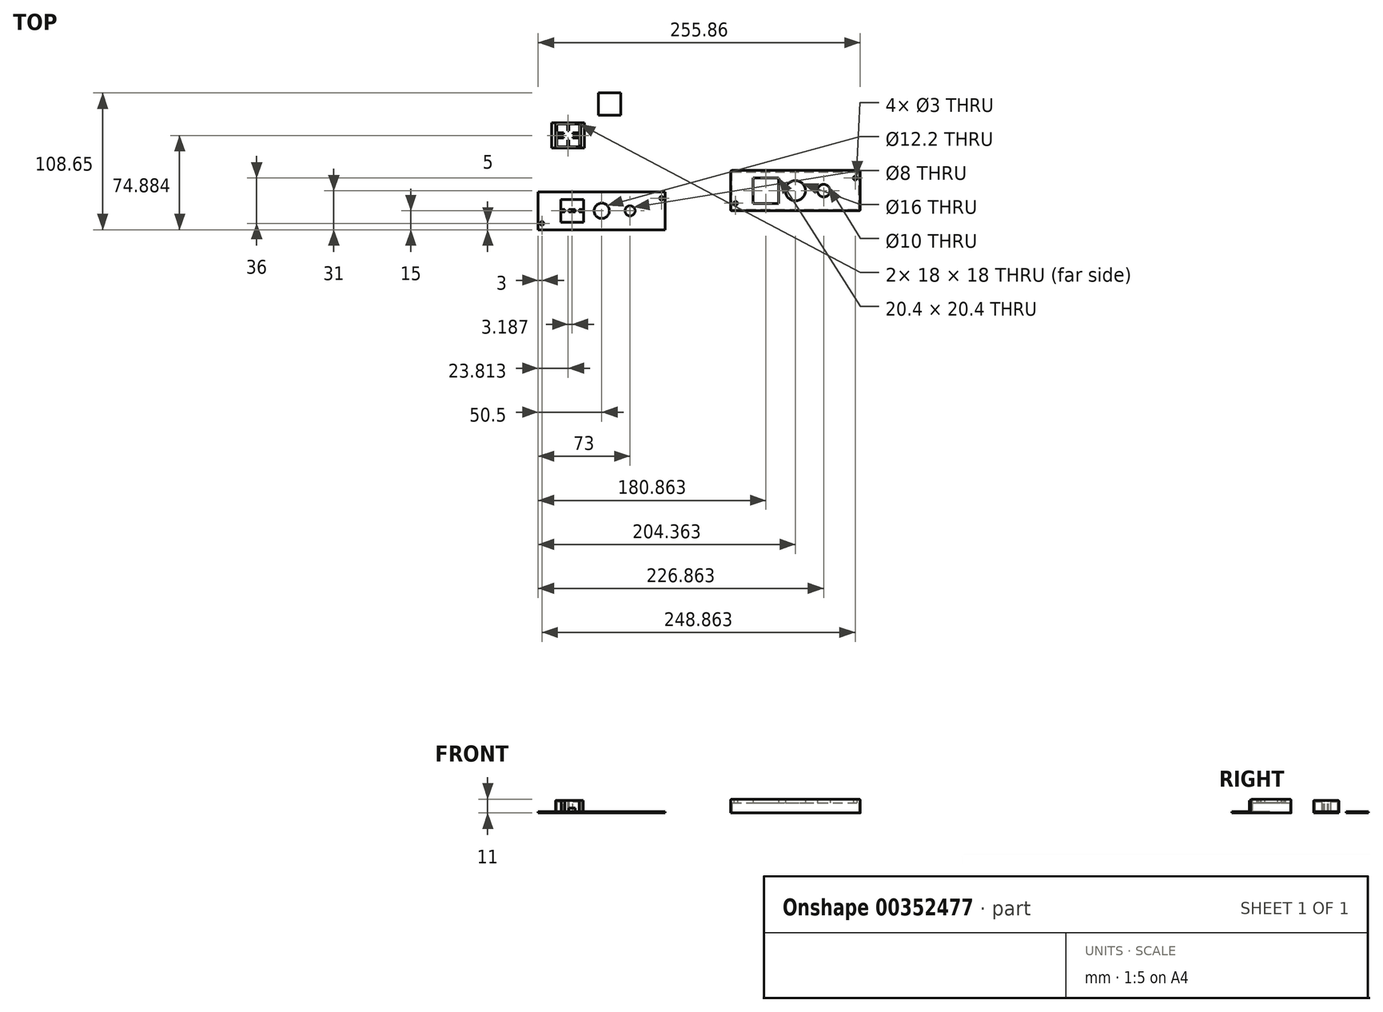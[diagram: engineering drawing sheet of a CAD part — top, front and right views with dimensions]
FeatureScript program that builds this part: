
annotation { "Feature Type Name" : "Feature", "Feature Type Description" : "" }
export const myFeature = defineFeature(function(context is Context, id is Id, definition is map)
    precondition{}
    {
        {
            var Q0;
            Q0=qCreatedBy(makeId("Top.planeOp"),FACE);
            var sketch = newSketch(context, id + "F0", { "sketchPlane" : qUnion([Q0])});
            skLineSegment(sketch, "E0.bottom", {"start": v(42.5, -14) * mm, "end": v(-42.5, -14) * mm, "construction": true});
            skLineSegment(sketch, "E0.top", {"start": v(42.5, 14) * mm, "end": v(-42.5, 14) * mm, "construction": true});
            skLineSegment(sketch, "E0.left", {"start": v(42.5, -14) * mm, "end": v(42.5, 14) * mm, "construction": true});
            skLineSegment(sketch, "E0.right", {"start": v(-42.5, -14) * mm, "end": v(-42.5, 14) * mm, "construction": true});
            skPoint(sketch, "E0.middle", {"position": v(0, 0) * mm});
            skCircle(sketch, "E1", {"center": v(-47.5, -10) * mm, "radius": 1.5 * mm});
            skCircle(sketch, "E2", {"center": v(47.5, 10) * mm, "radius": 1.5 * mm});
            skLineSegment(sketch, "E3.bottom", {"start": v(-50.5, 15) * mm, "end": v(50.5, 15) * mm});
            skLineSegment(sketch, "E3.top", {"start": v(-50.5, -15) * mm, "end": v(50.5, -15) * mm});
            skLineSegment(sketch, "E3.left", {"start": v(-50.5, 15) * mm, "end": v(-50.5, -15) * mm});
            skLineSegment(sketch, "E3.right", {"start": v(50.5, 15) * mm, "end": v(50.5, -15) * mm});
            skLineSegment(sketch, "E4.bottom", {"start": v(-32.5, 9) * mm, "end": v(-14.5, 9) * mm});
            skLineSegment(sketch, "E4.top", {"start": v(-32.5, -9) * mm, "end": v(-14.5, -9) * mm});
            skLineSegment(sketch, "E4.left", {"start": v(-32.5, 9) * mm, "end": v(-32.5, 1) * mm});
            skLineSegment(sketch, "E4.right", {"start": v(-14.5, 9) * mm, "end": v(-14.5, -9) * mm});
            skLineSegment(sketch, "E5.bottom", {"start": v(-29.25, 9) * mm, "end": v(-27.25, 9) * mm});
            skLineSegment(sketch, "E5.top", {"start": v(-29.25, -9) * mm, "end": v(-27.25, -9) * mm});
            skLineSegment(sketch, "E5.left", {"start": v(-29.25, 9) * mm, "end": v(-29.25, 1) * mm});
            skLineSegment(sketch, "E5.right", {"start": v(-27.25, 9) * mm, "end": v(-27.25, 1) * mm});
            skLineSegment(sketch, "E6.bottom", {"start": v(-19.75, 9) * mm, "end": v(-17.75, 9) * mm});
            skLineSegment(sketch, "E6.top", {"start": v(-19.75, -9) * mm, "end": v(-17.75, -9) * mm});
            skLineSegment(sketch, "E6.left", {"start": v(-19.75, 9) * mm, "end": v(-19.75, 1) * mm});
            skLineSegment(sketch, "E6.right", {"start": v(-17.75, 9) * mm, "end": v(-17.75, 1) * mm});
            skLineSegment(sketch, "E7.bottom", {"start": v(-32.5, 1) * mm, "end": v(-29.25, 1) * mm});
            skLineSegment(sketch, "E7.top", {"start": v(-32.5, -1) * mm, "end": v(-29.25, -1) * mm});
            skLineSegment(sketch, "E7.left", {"start": v(-32.5, 1) * mm, "end": v(-32.5, -1) * mm});
            skLineSegment(sketch, "E8.trimOffspring", {"start": v(-29.25, -1) * mm, "end": v(-29.25, -9) * mm});
            skLineSegment(sketch, "E9.trimOffspring", {"start": v(-27.25, 1) * mm, "end": v(-19.75, 1) * mm});
            skLineSegment(sketch, "E10.trimOffspring", {"start": v(-27.25, -1) * mm, "end": v(-27.25, -9) * mm});
            skLineSegment(sketch, "E11.trimOffspring", {"start": v(-27.25, -1) * mm, "end": v(-19.75, -1) * mm});
            skLineSegment(sketch, "E12.trimOffspring", {"start": v(-17.75, 1) * mm, "end": v(-14.5, 1) * mm});
            skLineSegment(sketch, "E13.trimOffspring", {"start": v(-17.75, -1) * mm, "end": v(-14.5, -1) * mm});
            skLineSegment(sketch, "E14.trimOffspring", {"start": v(-19.75, -1) * mm, "end": v(-19.75, -9) * mm});
            skLineSegment(sketch, "E15.trimOffspring", {"start": v(-17.75, -1) * mm, "end": v(-17.75, -9) * mm});
            skLineSegment(sketch, "E16.trimOffspring", {"start": v(-32.5, -1) * mm, "end": v(-32.5, -9) * mm});
            skCircle(sketch, "E17", {"center": v(0, 0) * mm, "radius": 6.1 * mm});
            skCircle(sketch, "E18", {"center": v(22.5, 0) * mm, "radius": 4 * mm});
            skSolve(sketch);
        }
        {
            var Q0;
            Q0=makeQuery(id+"F0.imprint","IMPRINT",FACE,{"disambiguationData":[TD([[makeQuery(id+"F0.imprint","IMPRINT",EDGE,{"derivedFrom":sQuery(id+"F0.wireOp",EDGE,"E1")}),-1.0]])]});
            var Q1;
            Q1=makeQuery(id+"F0.imprint","IMPRINT",FACE,{"disambiguationData":[TD([[makeQuery(id+"F0.imprint","IMPRINT",EDGE,{"derivedFrom":sQuery(id+"F0.wireOp",EDGE,"E5.bottom")}),-1.0]])]});
            extrude(context, id + "F1", {"entities" : qUnion([Q0, Q1]), "depth" : 1 * mm});
        }
        {
            var Q0;
            Q0=makeQuery(id+"F1.opExtrude","CAP_FACE",FACE,{"disambiguationData":[OSD([sQuery(id+"F0.wireOp",EDGE,"E1"),sQuery(id+"F0.wireOp",EDGE,"E2"),sQuery(id+"F0.wireOp",EDGE,"E3.bottom"),sQuery(id+"F0.wireOp",EDGE,"E3.top"),sQuery(id+"F0.wireOp",EDGE,"E3.left"),sQuery(id+"F0.wireOp",EDGE,"E3.right"),sQuery(id+"F0.wireOp",EDGE,"424KGZRB-5utR-a6Sk-f07y-1cyDiIB8TaRe"),sQuery(id+"F0.wireOp",EDGE,"xPdJMKwa-e6o6-zGCf-eMrl-vuys1Or93pA9"),sQuery(id+"F0.wireOp",EDGE,"E4.bottom"),sQuery(id+"F0.wireOp",EDGE,"E4.top"),sQuery(id+"F0.wireOp",EDGE,"E4.left"),sQuery(id+"F0.wireOp",EDGE,"E4.right"),sQuery(id+"F0.wireOp",EDGE,"E5.left"),sQuery(id+"F0.wireOp",EDGE,"E5.right"),sQuery(id+"F0.wireOp",EDGE,"E6.left"),sQuery(id+"F0.wireOp",EDGE,"E6.right"),sQuery(id+"F0.wireOp",EDGE,"E7.bottom"),sQuery(id+"F0.wireOp",EDGE,"E7.top"),sQuery(id+"F0.wireOp",EDGE,"E8.trimOffspring"),sQuery(id+"F0.wireOp",EDGE,"E9.trimOffspring"),sQuery(id+"F0.wireOp",EDGE,"E10.trimOffspring"),sQuery(id+"F0.wireOp",EDGE,"E11.trimOffspring"),sQuery(id+"F0.wireOp",EDGE,"E12.trimOffspring"),sQuery(id+"F0.wireOp",EDGE,"E13.trimOffspring"),sQuery(id+"F0.wireOp",EDGE,"E14.trimOffspring"),sQuery(id+"F0.wireOp",EDGE,"E15.trimOffspring"),sQuery(id+"F0.wireOp",EDGE,"E16.trimOffspring")])],"isStart":false});
            var sketch = newSketch(context, id + "F2", { "sketchPlane" : qUnion([Q0])});
            skLineSegment(sketch, "E19.bottom", {"start": v(-29.25, 1) * mm, "end": v(-32.25, 1) * mm});
            skLineSegment(sketch, "E19.top", {"start": v(-29.25, -1) * mm, "end": v(-32.25, -1) * mm});
            skLineSegment(sketch, "E19.left", {"start": v(-29.25, 1) * mm, "end": v(-29.25, -1) * mm});
            skLineSegment(sketch, "E19.right", {"start": v(-32.25, 1) * mm, "end": v(-32.25, -1) * mm});
            skLineSegment(sketch, "E20.bottom", {"start": v(-17.75, 1) * mm, "end": v(-14.75, 1) * mm});
            skLineSegment(sketch, "E20.top", {"start": v(-17.75, -1) * mm, "end": v(-14.75, -1) * mm});
            skLineSegment(sketch, "E20.left", {"start": v(-17.75, 1) * mm, "end": v(-17.75, -1) * mm});
            skLineSegment(sketch, "E20.right", {"start": v(-14.75, 1) * mm, "end": v(-14.75, -1) * mm});
            skSolve(sketch);
        }
        {
            var Q0;
            Q0 = qSketchRegion(id + "F2", true);
            extrude(context, id + "F3", {"entities" : qUnion([Q0]), "operationType" : NewBodyOperationType.ADD, "depth" : 9 * mm});
        }
        {
            var Q0;
            Q0=qCreatedBy(makeId("Top.planeOp"),FACE);
            var sketch = newSketch(context, id + "F4", { "sketchPlane" : qUnion([Q0])});
            skLineSegment(sketch, "E21.bottom", {"start": v(-36.69, 69.88) * mm, "end": v(-16.69, 69.88) * mm});
            skLineSegment(sketch, "E21.top", {"start": v(-36.69, 49.88) * mm, "end": v(-16.69, 49.88) * mm});
            skLineSegment(sketch, "E21.left", {"start": v(-36.69, 69.88) * mm, "end": v(-36.69, 49.88) * mm});
            skLineSegment(sketch, "E21.right", {"start": v(-16.69, 69.88) * mm, "end": v(-16.69, 49.88) * mm});
            skLineSegment(sketch, "E22.bottom", {"start": v(-2.69, 93.65) * mm, "end": v(15.11, 93.65) * mm});
            skLineSegment(sketch, "E22.top", {"start": v(-2.69, 75.85) * mm, "end": v(15.11, 75.85) * mm});
            skLineSegment(sketch, "E22.left", {"start": v(-2.69, 93.65) * mm, "end": v(-2.69, 75.85) * mm});
            skLineSegment(sketch, "E22.right", {"start": v(15.11, 93.65) * mm, "end": v(15.11, 75.85) * mm});
            skSolve(sketch);
        }
        {
            var Q0;
            Q0=makeQuery(id+"F4.imprint","IMPRINT",FACE,{"disambiguationData":[TD([[makeQuery(id+"F4.imprint","IMPRINT",EDGE,{"derivedFrom":sQuery(id+"F4.wireOp",EDGE,"E21.bottom")}),-1.0]])]});
            extrude(context, id + "F5", {"entities" : qUnion([Q0]), "depth" : 10 * mm});
        }
        {
            var Q0;
            Q0=makeQuery(id+"F5.opExtrude","CAP_FACE",FACE,{"disambiguationData":[OSD([sQuery(id+"F4.wireOp",EDGE,"E21.bottom"),sQuery(id+"F4.wireOp",EDGE,"E21.top"),sQuery(id+"F4.wireOp",EDGE,"E21.left"),sQuery(id+"F4.wireOp",EDGE,"E21.right")])],"isStart":true});
            shell(context, id + "F6", {"entities" : qUnion([Q0]), "thickness" : 1 * mm});
        }
        {
            var Q0;
            Q0=makeQuery(id+"F5.opExtrude","CAP_FACE",FACE,{"disambiguationData":[OSD([sQuery(id+"F4.wireOp",EDGE,"E21.bottom"),sQuery(id+"F4.wireOp",EDGE,"E21.top"),sQuery(id+"F4.wireOp",EDGE,"E21.left"),sQuery(id+"F4.wireOp",EDGE,"E21.right")])],"isStart":true});
            var sketch = newSketch(context, id + "F7", { "sketchPlane" : qUnion([Q0])});
            skLineSegment(sketch, "E23.bottom", {"start": v(-35.69, -57.88) * mm, "end": v(-27.19, -57.88) * mm});
            skLineSegment(sketch, "E23.top", {"start": v(-35.69, -58.58) * mm, "end": v(-27.19, -58.58) * mm});
            skLineSegment(sketch, "E23.left", {"start": v(-35.69, -57.88) * mm, "end": v(-35.69, -58.58) * mm});
            skLineSegment(sketch, "E23.right", {"start": v(-17.69, -57.88) * mm, "end": v(-17.69, -58.58) * mm});
            skLineSegment(sketch, "E24.bottom", {"start": v(-35.69, -61.18) * mm, "end": v(-27.19, -61.18) * mm});
            skLineSegment(sketch, "E24.top", {"start": v(-35.69, -61.88) * mm, "end": v(-27.19, -61.88) * mm});
            skLineSegment(sketch, "E24.left", {"start": v(-35.69, -61.18) * mm, "end": v(-35.69, -61.88) * mm});
            skLineSegment(sketch, "E24.right", {"start": v(-17.69, -61.18) * mm, "end": v(-17.69, -61.88) * mm});
            skLineSegment(sketch, "E25.bottom", {"start": v(-27.19, -50.88) * mm, "end": v(-26.19, -50.88) * mm});
            skLineSegment(sketch, "E25.top", {"start": v(-27.19, -68.88) * mm, "end": v(-26.19, -68.88) * mm});
            skLineSegment(sketch, "E25.left", {"start": v(-27.19, -50.88) * mm, "end": v(-27.19, -68.88) * mm});
            skLineSegment(sketch, "E25.right", {"start": v(-26.19, -50.88) * mm, "end": v(-26.19, -68.88) * mm});
            skLineSegment(sketch, "E26.trimOffspring", {"start": v(-26.19, -57.88) * mm, "end": v(-17.69, -57.88) * mm});
            skLineSegment(sketch, "E27.trimOffspring", {"start": v(-26.19, -58.58) * mm, "end": v(-17.69, -58.58) * mm});
            skLineSegment(sketch, "E28.trimOffspring", {"start": v(-26.19, -61.18) * mm, "end": v(-17.69, -61.18) * mm});
            skLineSegment(sketch, "E29.trimOffspring", {"start": v(-26.19, -61.88) * mm, "end": v(-17.69, -61.88) * mm});
            skSolve(sketch);
        }
        {
            var Q0;
            Q0 = qSketchRegion(id + "F7", true);
            extrude(context, id + "F8", {"entities" : qUnion([Q0]), "operationType" : NewBodyOperationType.ADD, "oppositeDirection" : true, "depth" : 9 * mm});
        }
        {
            var Q0;
            Q0=makeQuery(id+"F8.boolean.opBoolean","MERGE",FACE,{"derivedFrom":[makeQuery(id+"F5.opExtrude","CAP_FACE",FACE,{"disambiguationData":[OSD([sQuery(id+"F4.wireOp",EDGE,"E21.bottom"),sQuery(id+"F4.wireOp",EDGE,"E21.top"),sQuery(id+"F4.wireOp",EDGE,"E21.left"),sQuery(id+"F4.wireOp",EDGE,"E21.right")])],"isStart":true}),makeQuery(id+"F8.opExtrude","CAP_FACE",FACE,{"disambiguationData":[OSD([sQuery(id+"F7.wireOp",EDGE,"E23.bottom"),sQuery(id+"F7.wireOp",EDGE,"E23.top"),sQuery(id+"F7.wireOp",EDGE,"E23.left"),sQuery(id+"F7.wireOp",EDGE,"E23.right"),sQuery(id+"F7.wireOp",EDGE,"E24.bottom"),sQuery(id+"F7.wireOp",EDGE,"E24.top"),sQuery(id+"F7.wireOp",EDGE,"E24.left"),sQuery(id+"F7.wireOp",EDGE,"E24.right"),sQuery(id+"F7.wireOp",EDGE,"E25.bottom"),sQuery(id+"F7.wireOp",EDGE,"E25.top"),sQuery(id+"F7.wireOp",EDGE,"E25.left"),sQuery(id+"F7.wireOp",EDGE,"E25.right"),sQuery(id+"F7.wireOp",EDGE,"E26.trimOffspring"),sQuery(id+"F7.wireOp",EDGE,"E27.trimOffspring"),sQuery(id+"F7.wireOp",EDGE,"E28.trimOffspring"),sQuery(id+"F7.wireOp",EDGE,"E29.trimOffspring")])],"isStart":true})]});
            var sketch = newSketch(context, id + "F9", { "sketchPlane" : qUnion([Q0])});
            skLineSegment(sketch, "E30.bottom", {"start": v(-30.29, -56.28) * mm, "end": v(-23.09, -56.28) * mm});
            skLineSegment(sketch, "E30.top", {"start": v(-30.29, -63.48) * mm, "end": v(-23.09, -63.48) * mm});
            skLineSegment(sketch, "E30.left", {"start": v(-30.29, -56.28) * mm, "end": v(-30.29, -63.48) * mm});
            skLineSegment(sketch, "E30.right", {"start": v(-23.09, -56.28) * mm, "end": v(-23.09, -63.48) * mm});
            skSolve(sketch);
        }
        {
            var Q0;
            Q0 = qSketchRegion(id + "F9", true);
            extrude(context, id + "F10", {"entities" : qUnion([Q0]), "operationType" : NewBodyOperationType.REMOVE, "oppositeDirection" : true, "depth" : 9 * mm});
        }
        {
            var Q0;
            Q0=makeQuery(id+"F8.boolean.opBoolean","MERGE",FACE,{"derivedFrom":[makeQuery(id+"F5.opExtrude","CAP_FACE",FACE,{"disambiguationData":[OSD([sQuery(id+"F4.wireOp",EDGE,"E21.bottom"),sQuery(id+"F4.wireOp",EDGE,"E21.top"),sQuery(id+"F4.wireOp",EDGE,"E21.left"),sQuery(id+"F4.wireOp",EDGE,"E21.right")])],"isStart":true}),makeQuery(id+"F8.opExtrude","CAP_FACE",FACE,{"disambiguationData":[OSD([sQuery(id+"F7.wireOp",EDGE,"E23.bottom"),sQuery(id+"F7.wireOp",EDGE,"E23.top"),sQuery(id+"F7.wireOp",EDGE,"E23.left"),sQuery(id+"F7.wireOp",EDGE,"E23.right"),sQuery(id+"F7.wireOp",EDGE,"E24.bottom"),sQuery(id+"F7.wireOp",EDGE,"E24.top"),sQuery(id+"F7.wireOp",EDGE,"E24.left"),sQuery(id+"F7.wireOp",EDGE,"E24.right"),sQuery(id+"F7.wireOp",EDGE,"E25.bottom"),sQuery(id+"F7.wireOp",EDGE,"E25.top"),sQuery(id+"F7.wireOp",EDGE,"E25.left"),sQuery(id+"F7.wireOp",EDGE,"E25.right"),sQuery(id+"F7.wireOp",EDGE,"E26.trimOffspring"),sQuery(id+"F7.wireOp",EDGE,"E27.trimOffspring"),sQuery(id+"F7.wireOp",EDGE,"E28.trimOffspring"),sQuery(id+"F7.wireOp",EDGE,"E29.trimOffspring")])],"isStart":true})]});
            var sketch = newSketch(context, id + "F11", { "sketchPlane" : qUnion([Q0])});
            skLineSegment(sketch, "E31.bottom", {"start": v(-16.69, -69.88) * mm, "end": v(-13.69, -69.88) * mm});
            skLineSegment(sketch, "E31.top", {"start": v(-16.69, -49.88) * mm, "end": v(-13.69, -49.88) * mm});
            skLineSegment(sketch, "E31.left", {"start": v(-16.69, -69.88) * mm, "end": v(-16.69, -49.88) * mm});
            skLineSegment(sketch, "E31.right", {"start": v(-13.69, -69.88) * mm, "end": v(-13.69, -49.88) * mm});
            skLineSegment(sketch, "E32.bottom", {"start": v(-36.69, -69.88) * mm, "end": v(-39.69, -69.88) * mm});
            skLineSegment(sketch, "E32.top", {"start": v(-36.69, -49.88) * mm, "end": v(-39.69, -49.88) * mm});
            skLineSegment(sketch, "E32.left", {"start": v(-36.69, -69.88) * mm, "end": v(-36.69, -49.88) * mm});
            skLineSegment(sketch, "E32.right", {"start": v(-39.69, -69.88) * mm, "end": v(-39.69, -49.88) * mm});
            skSolve(sketch);
        }
        {
            var Q0;
            Q0=makeQuery(id+"F11.imprint","IMPRINT",FACE,{"disambiguationData":[TD([[makeQuery(id+"F11.imprint","IMPRINT",EDGE,{"derivedFrom":sQuery(id+"F11.wireOp",EDGE,"E32.bottom")}),-1.0]])]});
            var Q1;
            Q1=makeQuery(id+"F11.imprint","IMPRINT",FACE,{"disambiguationData":[TD([[makeQuery(id+"F11.imprint","IMPRINT",EDGE,{"derivedFrom":sQuery(id+"F11.wireOp",EDGE,"E31.bottom")}),1.0]])]});
            extrude(context, id + "F12", {"entities" : qUnion([Q0, Q1]), "operationType" : NewBodyOperationType.ADD, "oppositeDirection" : true, "depth" : 1 * mm});
        }
        {
            var Q0;
            Q0=makeQuery(id+"F5.opExtrude","CAP_FACE",FACE,{"disambiguationData":[OSD([sQuery(id+"F4.wireOp",EDGE,"E21.bottom"),sQuery(id+"F4.wireOp",EDGE,"E21.top"),sQuery(id+"F4.wireOp",EDGE,"E21.left"),sQuery(id+"F4.wireOp",EDGE,"E21.right")])],"isStart":false});
            var sketch = newSketch(context, id + "F13", { "sketchPlane" : qUnion([Q0])});
            skLineSegment(sketch, "E33.bottom", {"start": v(-35.69, 68.88) * mm, "end": v(-17.69, 68.88) * mm});
            skLineSegment(sketch, "E33.top", {"start": v(-35.69, 50.88) * mm, "end": v(-17.69, 50.88) * mm});
            skLineSegment(sketch, "E33.left", {"start": v(-35.69, 68.88) * mm, "end": v(-35.69, 50.88) * mm});
            skLineSegment(sketch, "E33.right", {"start": v(-17.69, 68.88) * mm, "end": v(-17.69, 50.88) * mm});
            skSolve(sketch);
        }
        {
            var Q0;
            Q0 = qSketchRegion(id + "F13", true);
            extrude(context, id + "F14", {"entities" : qUnion([Q0]), "operationType" : NewBodyOperationType.REMOVE, "oppositeDirection" : true, "depth" : 1 * mm});
        }
        {
            var Q0;
            Q0=makeQuery(id+"F5.opExtrude","SWEPT_EDGE",EDGE,{"disambiguationData":[OSD([sQuery(id+"F4.wireOp",EDGE,"E21.top"),sQuery(id+"F4.wireOp",EDGE,"E21.right")])]});
            var Q1;
            Q1=makeQuery(id+"F5.opExtrude","SWEPT_EDGE",EDGE,{"disambiguationData":[OSD([sQuery(id+"F4.wireOp",EDGE,"E21.bottom"),sQuery(id+"F4.wireOp",EDGE,"E21.right")])]});
            var Q2;
            Q2=makeQuery(id+"F5.opExtrude","CAP_EDGE",EDGE,{"disambiguationData":[OSD([sQuery(id+"F4.wireOp",EDGE,"E21.right")])],"isStart":false});
            var Q3;
            Q3=makeQuery(id+"F5.opExtrude","CAP_EDGE",EDGE,{"disambiguationData":[OSD([sQuery(id+"F4.wireOp",EDGE,"E21.bottom")])],"isStart":false});
            var Q4;
            Q4=makeQuery(id+"F5.opExtrude","CAP_EDGE",EDGE,{"disambiguationData":[OSD([sQuery(id+"F4.wireOp",EDGE,"E21.top")])],"isStart":false});
            var Q5;
            Q5=makeQuery(id+"F5.opExtrude","CAP_EDGE",EDGE,{"disambiguationData":[OSD([sQuery(id+"F4.wireOp",EDGE,"E21.left")])],"isStart":false});
            var Q6;
            Q6=makeQuery(id+"F5.opExtrude","SWEPT_EDGE",EDGE,{"disambiguationData":[OSD([sQuery(id+"F4.wireOp",EDGE,"E21.top"),sQuery(id+"F4.wireOp",EDGE,"E21.left")])]});
            var Q7;
            Q7=makeQuery(id+"F5.opExtrude","SWEPT_EDGE",EDGE,{"disambiguationData":[OSD([sQuery(id+"F4.wireOp",EDGE,"E21.bottom"),sQuery(id+"F4.wireOp",EDGE,"E21.left")])]});
            fillet(context, id + "F15", {"entities" : qUnion([Q0, Q1, Q2, Q3, Q4, Q5, Q6, Q7]), "radius" : 0.5 * mm, "tangentPropagation" : true, "allowEdgeOverflow" : false});
        }
        {
            var Q0;
            Q0=makeQuery(id+"F4.imprint","IMPRINT",FACE,{"disambiguationData":[TD([[makeQuery(id+"F4.imprint","IMPRINT",EDGE,{"derivedFrom":sQuery(id+"F4.wireOp",EDGE,"E22.bottom")}),-1.0]])]});
            extrude(context, id + "F16", {"entities" : qUnion([Q0]), "depth" : 1 * mm});
        }
        {
            var Q0;
            Q0=makeQuery(id+"F1.opExtrude","CAP_FACE",FACE,{"disambiguationData":[OSD([sQuery(id+"F0.wireOp",EDGE,"E1"),sQuery(id+"F0.wireOp",EDGE,"E2"),sQuery(id+"F0.wireOp",EDGE,"E3.bottom"),sQuery(id+"F0.wireOp",EDGE,"E3.top"),sQuery(id+"F0.wireOp",EDGE,"E3.left"),sQuery(id+"F0.wireOp",EDGE,"E3.right"),sQuery(id+"F0.wireOp",EDGE,"424KGZRB-5utR-a6Sk-f07y-1cyDiIB8TaRe"),sQuery(id+"F0.wireOp",EDGE,"xPdJMKwa-e6o6-zGCf-eMrl-vuys1Or93pA9"),sQuery(id+"F0.wireOp",EDGE,"E4.bottom"),sQuery(id+"F0.wireOp",EDGE,"E4.top"),sQuery(id+"F0.wireOp",EDGE,"E4.left"),sQuery(id+"F0.wireOp",EDGE,"E4.right"),sQuery(id+"F0.wireOp",EDGE,"E5.left"),sQuery(id+"F0.wireOp",EDGE,"E5.right"),sQuery(id+"F0.wireOp",EDGE,"E6.left"),sQuery(id+"F0.wireOp",EDGE,"E6.right"),sQuery(id+"F0.wireOp",EDGE,"E7.bottom"),sQuery(id+"F0.wireOp",EDGE,"E7.top"),sQuery(id+"F0.wireOp",EDGE,"E8.trimOffspring"),sQuery(id+"F0.wireOp",EDGE,"E9.trimOffspring"),sQuery(id+"F0.wireOp",EDGE,"E10.trimOffspring"),sQuery(id+"F0.wireOp",EDGE,"E11.trimOffspring"),sQuery(id+"F0.wireOp",EDGE,"E12.trimOffspring"),sQuery(id+"F0.wireOp",EDGE,"E13.trimOffspring"),sQuery(id+"F0.wireOp",EDGE,"E14.trimOffspring"),sQuery(id+"F0.wireOp",EDGE,"E15.trimOffspring"),sQuery(id+"F0.wireOp",EDGE,"E16.trimOffspring")])],"isStart":false});
            var sketch = newSketch(context, id + "F17", { "sketchPlane" : qUnion([Q0])});
            skLineSegment(sketch, "E34.bottom", {"start": v(-26, 1) * mm, "end": v(-21, 1) * mm});
            skLineSegment(sketch, "E34.top", {"start": v(-26, -1) * mm, "end": v(-21, -1) * mm});
            skLineSegment(sketch, "E34.left", {"start": v(-26, 1) * mm, "end": v(-26, -1) * mm});
            skLineSegment(sketch, "E34.right", {"start": v(-21, 1) * mm, "end": v(-21, -1) * mm});
            skSolve(sketch);
        }
        {
            var Q0;
            Q0 = qSketchRegion(id + "F17", true);
            extrude(context, id + "F18", {"entities" : qUnion([Q0]), "operationType" : NewBodyOperationType.ADD, "depth" : 3 * mm});
        }
        {
            var Q0;
            Q0=qCreatedBy(makeId("Top.planeOp"),FACE);
            var sketch = newSketch(context, id + "F19", { "sketchPlane" : qUnion([Q0])});
            skLineSegment(sketch, "E35.bottom", {"start": v(103.36, 32) * mm, "end": v(204.36, 32) * mm, "construction": true});
            skLineSegment(sketch, "E35.top", {"start": v(103.36, 0) * mm, "end": v(204.36, 0) * mm, "construction": true});
            skLineSegment(sketch, "E35.left", {"start": v(103.36, 32) * mm, "end": v(103.36, 0) * mm, "construction": true});
            skLineSegment(sketch, "E35.right", {"start": v(204.36, 32) * mm, "end": v(204.36, 0) * mm, "construction": true});
            skLineSegment(sketch, "E36.bottom", {"start": v(102.36, 32) * mm, "end": v(205.36, 32) * mm});
            skLineSegment(sketch, "E36.top", {"start": v(102.36, 0) * mm, "end": v(205.36, 0) * mm});
            skLineSegment(sketch, "E36.left", {"start": v(102.36, 32) * mm, "end": v(102.36, 0) * mm});
            skLineSegment(sketch, "E36.right", {"start": v(205.36, 32) * mm, "end": v(205.36, 0) * mm});
            skCircle(sketch, "E37", {"center": v(106.36, 6) * mm, "radius": 1.5 * mm});
            skCircle(sketch, "E38", {"center": v(201.36, 26) * mm, "radius": 1.5 * mm});
            skCircle(sketch, "E39", {"center": v(153.86, 16) * mm, "radius": 8 * mm});
            skCircle(sketch, "E40", {"center": v(176.36, 16) * mm, "radius": 5 * mm});
            skLineSegment(sketch, "E41.bottom", {"start": v(140.56, 5.8) * mm, "end": v(120.16, 5.8) * mm});
            skLineSegment(sketch, "E41.top", {"start": v(140.56, 26.2) * mm, "end": v(120.16, 26.2) * mm});
            skLineSegment(sketch, "E41.left", {"start": v(140.56, 5.8) * mm, "end": v(140.56, 26.2) * mm});
            skLineSegment(sketch, "E41.right", {"start": v(120.16, 5.8) * mm, "end": v(120.16, 26.2) * mm});
            skPoint(sketch, "E41.middle", {"position": v(130.36, 16) * mm});
            skSolve(sketch);
        }
        {
            var Q0;
            Q0 = qSketchRegion(id + "F19", true);
            extrude(context, id + "F20", {"entities" : qUnion([Q0]), "depth" : 11 * mm});
        }
        {
            var Q0;
            Q0=makeQuery(id+"F20.opExtrude","CAP_FACE",FACE,{"disambiguationData":[OSD([sQuery(id+"F19.wireOp",EDGE,"E36.bottom"),sQuery(id+"F19.wireOp",EDGE,"E36.top"),sQuery(id+"F19.wireOp",EDGE,"E36.left"),sQuery(id+"F19.wireOp",EDGE,"E36.right"),sQuery(id+"F19.wireOp",EDGE,"E37"),sQuery(id+"F19.wireOp",EDGE,"E38"),sQuery(id+"F19.wireOp",EDGE,"RyGLUrYX-1u43-e16M-MsOJ-A2O3aQofN9jR.bottom"),sQuery(id+"F19.wireOp",EDGE,"RyGLUrYX-1u43-e16M-MsOJ-A2O3aQofN9jR.top"),sQuery(id+"F19.wireOp",EDGE,"RyGLUrYX-1u43-e16M-MsOJ-A2O3aQofN9jR.left"),sQuery(id+"F19.wireOp",EDGE,"RyGLUrYX-1u43-e16M-MsOJ-A2O3aQofN9jR.right")])],"isStart":true});
            var sketch = newSketch(context, id + "F21", { "sketchPlane" : qUnion([Q0])});
            skLineSegment(sketch, "E42.bottom", {"start": v(103.36, -1) * mm, "end": v(204.36, -1) * mm});
            skLineSegment(sketch, "E42.top", {"start": v(103.36, -31) * mm, "end": v(204.36, -31) * mm});
            skLineSegment(sketch, "E42.left", {"start": v(103.36, -1) * mm, "end": v(103.36, -31) * mm});
            skLineSegment(sketch, "E42.right", {"start": v(204.36, -1) * mm, "end": v(204.36, -31) * mm});
            skSolve(sketch);
        }
        {
            var Q0;
            Q0 = qSketchRegion(id + "F21", true);
            extrude(context, id + "F22", {"entities" : qUnion([Q0]), "operationType" : NewBodyOperationType.REMOVE, "oppositeDirection" : true, "depth" : 8 * mm});
        }
        {
            var Q0;
            Q0=makeQuery(id+"F20.opExtrude","CAP_EDGE",EDGE,{"disambiguationData":[OSD([sQuery(id+"F19.wireOp",EDGE,"E36.left")])],"isStart":false});
            var Q1;
            Q1=makeQuery(id+"F20.opExtrude","CAP_EDGE",EDGE,{"disambiguationData":[OSD([sQuery(id+"F19.wireOp",EDGE,"E36.bottom")])],"isStart":false});
            var Q2;
            Q2=makeQuery(id+"F20.opExtrude","CAP_EDGE",EDGE,{"disambiguationData":[OSD([sQuery(id+"F19.wireOp",EDGE,"E36.top")])],"isStart":false});
            var Q3;
            Q3=makeQuery(id+"F20.opExtrude","CAP_EDGE",EDGE,{"disambiguationData":[OSD([sQuery(id+"F19.wireOp",EDGE,"E36.right")])],"isStart":false});
            var Q4;
            Q4=makeQuery(id+"F20.opExtrude","SWEPT_EDGE",EDGE,{"disambiguationData":[OSD([sQuery(id+"F19.wireOp",EDGE,"E36.bottom"),sQuery(id+"F19.wireOp",EDGE,"E36.right")])]});
            var Q5;
            Q5=makeQuery(id+"F20.opExtrude","SWEPT_EDGE",EDGE,{"disambiguationData":[OSD([sQuery(id+"F19.wireOp",EDGE,"E36.top"),sQuery(id+"F19.wireOp",EDGE,"E36.right")])]});
            var Q6;
            Q6=makeQuery(id+"F20.opExtrude","SWEPT_EDGE",EDGE,{"disambiguationData":[OSD([sQuery(id+"F19.wireOp",EDGE,"E36.bottom"),sQuery(id+"F19.wireOp",EDGE,"E36.left")])]});
            var Q7;
            Q7=makeQuery(id+"F20.opExtrude","SWEPT_EDGE",EDGE,{"disambiguationData":[OSD([sQuery(id+"F19.wireOp",EDGE,"E36.top"),sQuery(id+"F19.wireOp",EDGE,"E36.left")])]});
            fillet(context, id + "F23", {"entities" : qUnion([Q0, Q1, Q2, Q3, Q4, Q5, Q6, Q7]), "radius" : 1 * mm, "tangentPropagation" : true, "allowEdgeOverflow" : false});
        }
    });
